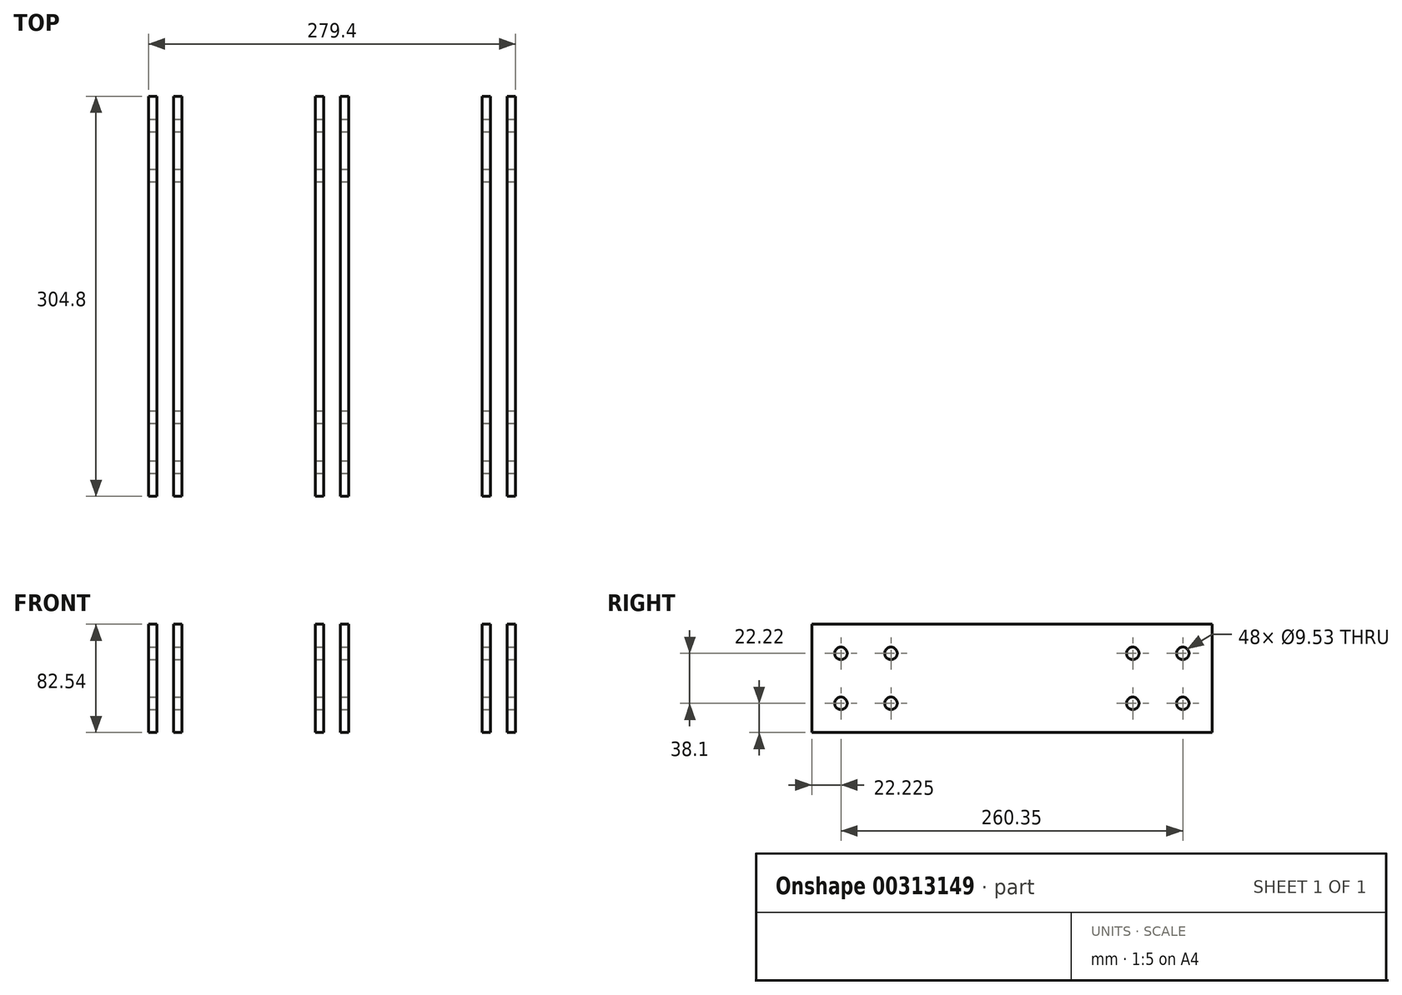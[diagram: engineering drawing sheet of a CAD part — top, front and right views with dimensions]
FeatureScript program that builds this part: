
annotation { "Feature Type Name" : "Feature", "Feature Type Description" : "" }
export const myFeature = defineFeature(function(context is Context, id is Id, definition is map)
    precondition{}
    {
        {
            var Q0;
            Q0=qCreatedBy(makeId("Top.planeOp"),FACE);
            var sketch = newSketch(context, id + "F0", { "sketchPlane" : qUnion([Q0])});
            skLineSegment(sketch, "E0.bottom", {"start": v(0, 0) * mm, "end": v(6.35, 0) * mm});
            skLineSegment(sketch, "E0.top", {"start": v(0, 304.8) * mm, "end": v(6.35, 304.8) * mm});
            skLineSegment(sketch, "E0.left", {"start": v(0, 0) * mm, "end": v(0, 304.8) * mm});
            skLineSegment(sketch, "E0.right", {"start": v(6.35, 0) * mm, "end": v(6.35, 304.8) * mm});
            skLineSegment(sketch, "E1.bottom", {"start": v(19.05, 0) * mm, "end": v(25.4, 0) * mm});
            skLineSegment(sketch, "E1.top", {"start": v(19.05, 304.8) * mm, "end": v(25.4, 304.8) * mm});
            skLineSegment(sketch, "E1.left", {"start": v(19.05, 0) * mm, "end": v(19.05, 304.8) * mm});
            skLineSegment(sketch, "E1.right", {"start": v(25.4, 0) * mm, "end": v(25.4, 304.8) * mm});
            skLineSegment(sketch, "E2.1.0.0", {"start": v(127, 0) * mm, "end": v(127, 304.8) * mm});
            skLineSegment(sketch, "E2.1.0.1", {"start": v(133.35, 0) * mm, "end": v(133.35, 304.8) * mm});
            skLineSegment(sketch, "E2.1.0.2", {"start": v(146.05, 0) * mm, "end": v(146.05, 304.8) * mm});
            skLineSegment(sketch, "E2.1.0.3", {"start": v(152.4, 0) * mm, "end": v(152.4, 304.8) * mm});
            skLineSegment(sketch, "E2.1.0.4", {"start": v(127, 0) * mm, "end": v(133.35, 0) * mm});
            skLineSegment(sketch, "E2.1.0.5", {"start": v(127, 304.8) * mm, "end": v(133.35, 304.8) * mm});
            skLineSegment(sketch, "E2.1.0.6", {"start": v(146.05, 0) * mm, "end": v(152.4, 0) * mm});
            skLineSegment(sketch, "E2.1.0.7", {"start": v(146.05, 304.8) * mm, "end": v(152.4, 304.8) * mm});
            skLineSegment(sketch, "E2.2.0.0", {"start": v(254, 0) * mm, "end": v(254, 304.8) * mm});
            skLineSegment(sketch, "E2.2.0.1", {"start": v(260.35, 0) * mm, "end": v(260.35, 304.8) * mm});
            skLineSegment(sketch, "E2.2.0.2", {"start": v(273.05, 0) * mm, "end": v(273.05, 304.8) * mm});
            skLineSegment(sketch, "E2.2.0.3", {"start": v(279.4, 0) * mm, "end": v(279.4, 304.8) * mm});
            skLineSegment(sketch, "E2.2.0.4", {"start": v(254, 0) * mm, "end": v(260.35, 0) * mm});
            skLineSegment(sketch, "E2.2.0.5", {"start": v(254, 304.8) * mm, "end": v(260.35, 304.8) * mm});
            skLineSegment(sketch, "E2.2.0.6", {"start": v(273.05, 0) * mm, "end": v(279.4, 0) * mm});
            skLineSegment(sketch, "E2.2.0.7", {"start": v(273.05, 304.8) * mm, "end": v(279.4, 304.8) * mm});
            skLineSegment(sketch, "E2.direction1", {"start": v(0, 0) * mm, "end": v(127, 0) * mm, "construction": true});
            skSolve(sketch);
        }
        {
            var Q0;
            Q0 = qSketchRegion(id + "F0", true);
            extrude(context, id + "F1", {"entities" : qUnion([Q0]), "endBound" : BoundingType.SYMMETRIC, "depth" : 82.55 * mm});
        }
        {
            var Q0;
            Q0=makeQuery(id+"F1.opExtrude","SWEPT_FACE",FACE,{"disambiguationData":[OSD([sQuery(id+"F0.wireOp",EDGE,"E1.right")])]});
            var sketch = newSketch(context, id + "F2", { "sketchPlane" : qUnion([Q0])});
            skCircle(sketch, "E3", {"center": v(282.58, 19.05) * mm, "radius": 4.76 * mm});
            skCircle(sketch, "E4", {"center": v(282.58, -19.05) * mm, "radius": 4.76 * mm});
            skCircle(sketch, "E5", {"center": v(244.48, -19.05) * mm, "radius": 4.76 * mm});
            skCircle(sketch, "E6", {"center": v(244.48, 19.05) * mm, "radius": 4.76 * mm});
            skCircle(sketch, "E7.1.0.0", {"center": v(60.32, 19.05) * mm, "radius": 4.76 * mm});
            skCircle(sketch, "E7.1.0.1", {"center": v(60.32, -19.05) * mm, "radius": 4.76 * mm});
            skCircle(sketch, "E7.1.0.2", {"center": v(22.22, -19.05) * mm, "radius": 4.76 * mm});
            skCircle(sketch, "E7.1.0.3", {"center": v(22.22, 19.05) * mm, "radius": 4.76 * mm});
            skSolve(sketch);
        }
        {
            var Q0;
            Q0 = qSketchRegion(id + "F2", true);
            extrude(context, id + "F3", {"entities" : qUnion([Q0]), "operationType" : NewBodyOperationType.REMOVE, "endBound" : BoundingType.THROUGH_ALL, "oppositeDirection" : true, "depth" : 25.4 * mm, "hasSecondDirection" : true, "secondDirectionBound" : SecondDirectionBoundingType.THROUGH_ALL, "secondDirectionOppositeDirection" : false, "secondDirectionDepth" : 25.4 * mm});
        }
    });
